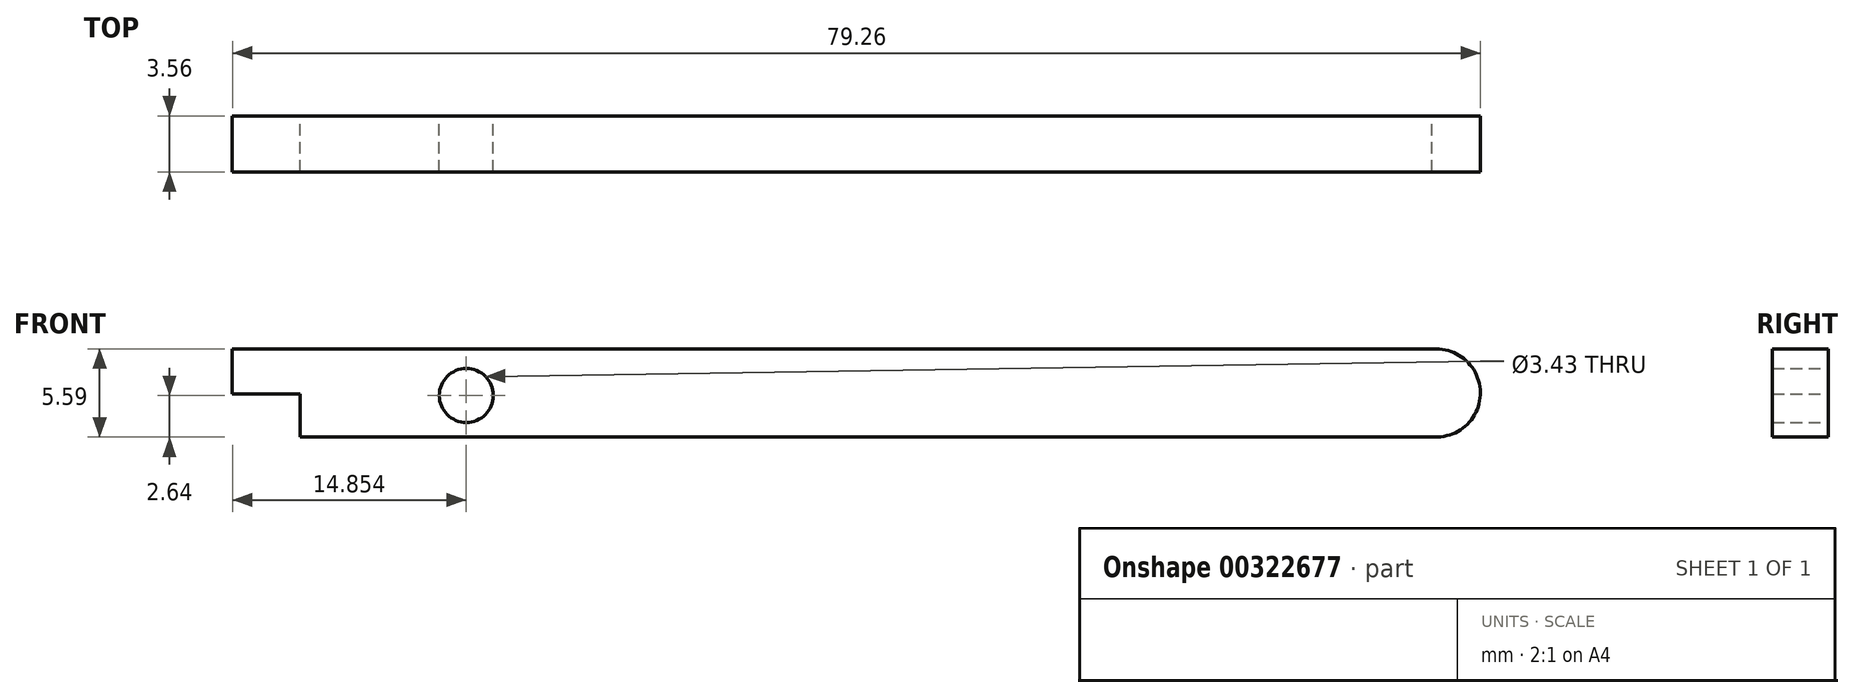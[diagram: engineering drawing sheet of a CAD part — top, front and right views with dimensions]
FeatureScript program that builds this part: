
annotation { "Feature Type Name" : "Feature", "Feature Type Description" : "" }
export const myFeature = defineFeature(function(context is Context, id is Id, definition is map)
    precondition{}
    {
        {
            var Q0;
            Q0=qCreatedBy(makeId("Front.planeOp"),FACE);
            var sketch = newSketch(context, id + "F0", { "sketchPlane" : qUnion([Q0])});
            skLineSegment(sketch, "E0", {"start": v(-15.86, 26.97) * mm, "end": v(60.6, 26.97) * mm});
            skLineSegment(sketch, "E1", {"start": v(-15.86, 26.97) * mm, "end": v(-15.86, 24.12) * mm});
            skLineSegment(sketch, "E2", {"start": v(-15.86, 24.12) * mm, "end": v(-11.55, 24.12) * mm});
            skLineSegment(sketch, "E3", {"start": v(-11.55, 24.12) * mm, "end": v(-11.55, 21.4) * mm});
            skLineSegment(sketch, "E4", {"start": v(-11.55, 21.4) * mm, "end": v(60.34, 21.4) * mm});
            skArc(sketch, "E5", {"start": v(60.34, 21.4) * mm, "mid": v(63.4, 24.04) * mm, "end": v(60.6, 26.97) * mm});
            skCircle(sketch, "E6", {"center": v(-1, 24.02) * mm, "radius": 1.71 * mm});
            skSolve(sketch);
        }
        {
            var Q0;
            Q0=makeQuery(id+"F0.imprint","IMPRINT",FACE,{"disambiguationData":[TD([[makeQuery(id+"F0.imprint","IMPRINT",EDGE,{"derivedFrom":sQuery(id+"F0.wireOp",EDGE,"E0")}),-1.0]])]});
            extrude(context, id + "F1", {"entities" : qUnion([Q0]), "depth" : 3.56 * mm});
        }
    });
